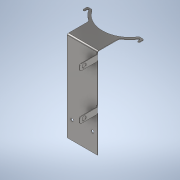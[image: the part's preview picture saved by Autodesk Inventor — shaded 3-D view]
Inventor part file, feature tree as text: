
AUTODESK INVENTOR PART (.ipt)
format: ipt  version: 2020.3 (Build 243373000, 373)  size: 321,024 bytes
history: native  units: mm
features: sheet_metal_op x8, sketch x7, chamfer x5, other x4, hole x2, extrude x1, fillet x1
ambient origin geometry x8: Origin, YZ Plane, XZ Plane, XY Plane, X Axis, Y Axis, Z Axis, Center Point
bodies: Solid1 (feature_tree)
feature tree (28):
  sheet_metal_op  "Face1"
  sheet_metal_op  "Flange1"
  sheet_metal_op  "Face2"
  chamfer  "Corner Round7"
  extrude  "Extrusion1"  Depth=150.0mm
  sketch  "Sketch5"  dims[d7=79.0mm d8=90.0deg d9=1.0mm]
  hole  "Hole1"  [1 undecoded]
  chamfer  "Corner Round12"
  chamfer  "Corner Round13"
  chamfer  "Corner Round14"
  chamfer  "Corner Round15"
  sheet_metal_op  "Face4"
  hole  "Hole2"  [1 undecoded]
  fillet  "Fillet1"  Radius=1.0mm
  sketch  "Sketch1"  dims[d0=50.0mm d1=150.0mm]
  other  "Plate1"
  sketch  "Sketch2"  dims[d2=1.0mm d3=1.0mm]
  other  "Plate2"
  sheet_metal_op  "Bend1"
  sheet_metal_op  "Corner1"
  sketch  "Sketch4"  dims[d4=0.5mm d5=2.0mm d6=1.0mm]
  other  "Plate3"
  sheet_metal_op  "Bend2"
  sketch  "Sketch7"  dims[d10=4.0mm]
  sketch  "Sketch13"  dims[d11=1.0mm]
  other  "Plate5"
  sheet_metal_op  "Bend4"
  sketch  "Sketch14"  dims[d12=1.0mm d13=91.0mm d14=40.0mm d15=40.0mm d16=40.0mm d17=40.0mm d18=1.0mm d19=1.0mm d20=0.5mm d21=2.0mm d22=1.0mm d23=0.0mm d24=0.0mm d30=9.0mm d31=109.0mm d37=30.0mm d38=8.0mm d39=8.0mm d40=4.5mm d41=4.5mm d42=4.0mm d43=2.0mm d44=90.0deg d45=1.0mm d46=20.594885mm d61=6.0mm d84=22.0mm d85=8.0mm d86=0.0mm d87=8.0mm d88=3.0mm d89=8.0mm d90=180.0deg d91=8.0mm d92=90.0deg d93=3.0mm d95=5.0mm d96=5.0mm d97=2.0mm d98=1.5mm d99=1.5mm d100=1.0mm d101=2.0mm d102=1.5mm d103=1.0mm d104=1.0mm d105=1.0mm d106=3.0mm d107=3.0mm d109=92.6mm d115=1.3mm d116=1.3mm d117=45.792087mm d118=6.839208mm d119=1.3mm d120=1.3mm d121=45.792087mm d133=30.0mm d134=10.0mm d135=146.0mm d136=30.0mm d137=10.0mm d138=66.0mm d139=1.0mm d140=1.0mm d141=0.5mm d142=2.0mm d143=1.0mm d144=23.0mm d145=5.0mm d146=5.0mm d147=7.0mm d148=6.0mm d149=4.0mm d150=2.0mm d151=90.0deg d152=1.0mm d153=20.594885mm d154=76.0mm d155=2.0mm]
note: 2 required parameter values undecoded (feature->parameter linkage not recoverable at this tier; creation-order binding heuristic only, values carry confidence <= 0.55)
